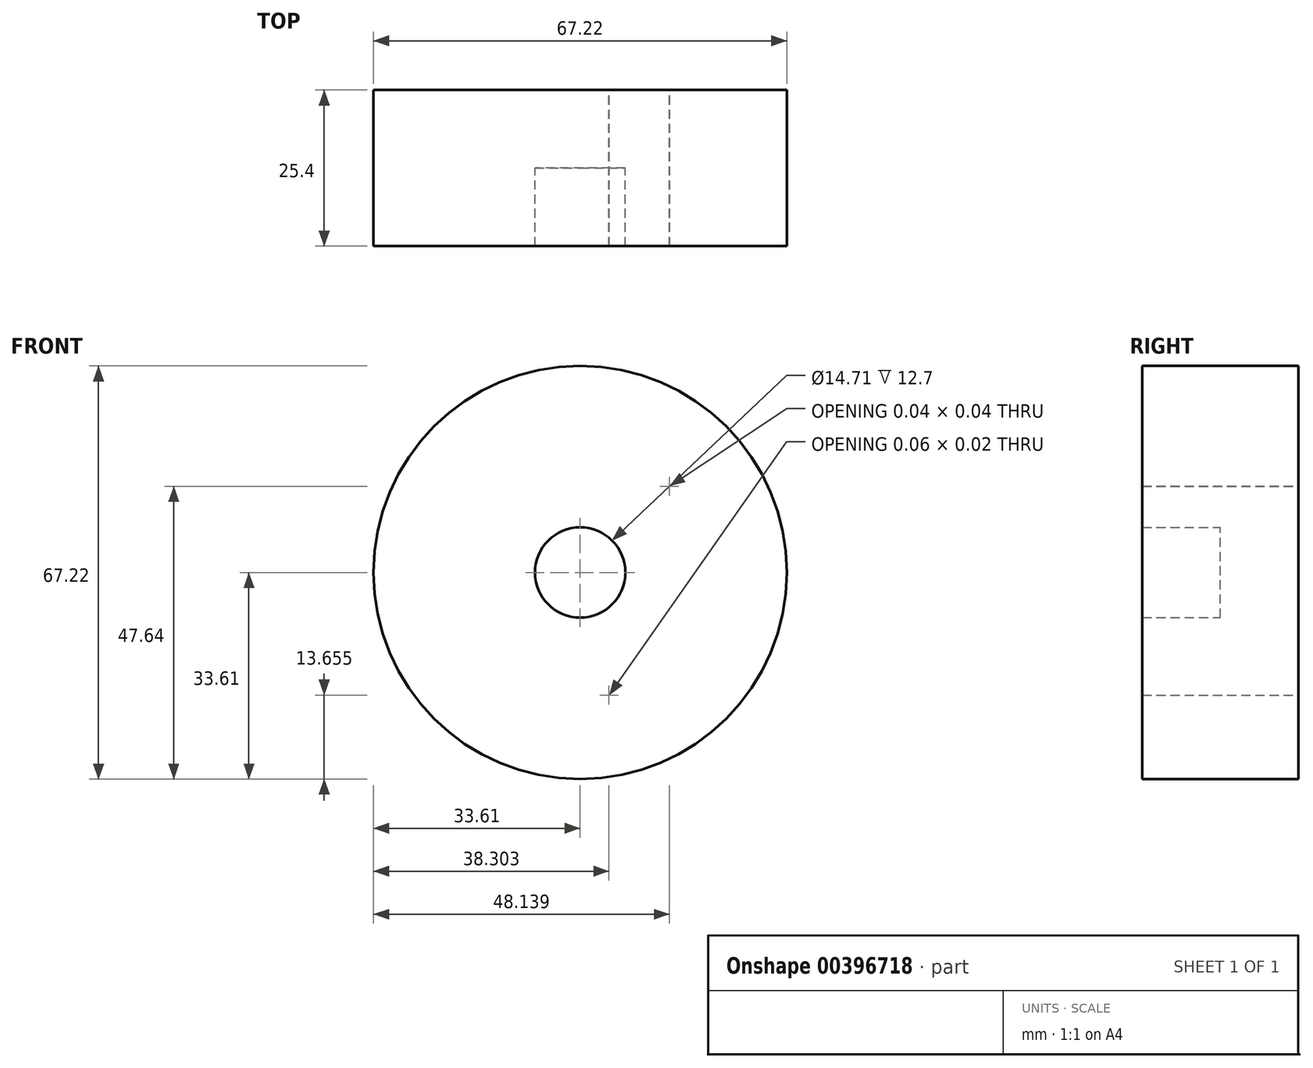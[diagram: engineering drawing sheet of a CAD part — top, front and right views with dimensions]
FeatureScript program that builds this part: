
annotation { "Feature Type Name" : "Feature", "Feature Type Description" : "" }
export const myFeature = defineFeature(function(context is Context, id is Id, definition is map)
    precondition{}
    {
        {
            var Q0;
            Q0=qCreatedBy(makeId("Front.planeOp"),FACE);
            var sketch = newSketch(context, id + "F0", { "sketchPlane" : qUnion([Q0])});
            skCircle(sketch, "E0", {"center": v(0, 0) * mm, "radius": 33.61 * mm});
            skCircle(sketch, "E1", {"center": v(0, 0) * mm, "radius": 7.35 * mm});
            skArc(sketch, "E2", {"start": v(14.55, 14) * mm, "mid": v(14.53, 14.03) * mm, "end": v(14.52, 14.05) * mm});
            skArc(sketch, "E3", {"start": v(14.55, 14) * mm, "mid": v(14.53, 14.03) * mm, "end": v(14.5, 14.05) * mm});
            skArc(sketch, "E4", {"start": v(14.52, 14.05) * mm, "mid": v(14.51, 14.05) * mm, "end": v(14.5, 14.05) * mm});
            skArc(sketch, "E5", {"start": v(4.66, -19.97) * mm, "mid": v(4.7, -19.96) * mm, "end": v(4.72, -19.95) * mm});
            skPoint(sketch, "E6.endSnap0", {"position": v(-19.51, 5.12) * mm});
            skArc(sketch, "E7", {"start": v(4.66, -19.97) * mm, "mid": v(4.7, -19.95) * mm, "end": v(4.72, -19.94) * mm});
            skArc(sketch, "E8", {"start": v(4.72, -19.95) * mm, "mid": v(4.72, -19.95) * mm, "end": v(4.72, -19.94) * mm});
            skPoint(sketch, "E9.orphan", {"position": v(0, 7.35) * mm});
            skPoint(sketch, "E10.end.orphan", {"position": v(18.76, 5.12) * mm});
            skPoint(sketch, "E11.orphan", {"position": v(0, -33.61) * mm});
            skPoint(sketch, "E12.start.orphan", {"position": v(-5.05, -19.97) * mm});
            skSolve(sketch);
        }
        {
            var Q0;
            {var subQ0=sQuery(id+"F0.wireOp",EDGE,"ypr8OIAr-gZSa-dfjQ-iwGS-s2g7RQJyGAwi");Q0=makeQuery(id+"F0.imprint","IMPRINT",FACE,{"disambiguationData":[TD([[makeQuery(id+"F0.imprint","IMPRINT",EDGE,{"derivedFrom":subQ0}),-1.0]])]});}
            var Q1;
            {var subQ0=sQuery(id+"F0.wireOp",EDGE,"pcJwF8Lj-ccY8-LTFF-dTaw-QFjFHTA8a31K");Q1=makeQuery(id+"F0.imprint","IMPRINT",FACE,{"disambiguationData":[TD([[makeQuery(id+"F0.imprint","IMPRINT",EDGE,{"derivedFrom":subQ0}),-1.0]])]});}
            var Q2;
            {var subQ0=sQuery(id+"F0.wireOp",EDGE,"55HTWmI2-19od-qPii-Hjk4-NtNte6FnF2xr");Q2=makeQuery(id+"F0.imprint","IMPRINT",FACE,{"disambiguationData":[TD([[makeQuery(id+"F0.imprint","IMPRINT",EDGE,{"derivedFrom":subQ0}),-1.0]])]});}
            var Q3;
            {var subQ0=sQuery(id+"F0.wireOp",EDGE,"E12");Q3=makeQuery(id+"F0.imprint","IMPRINT",FACE,{"disambiguationData":[TD([[makeQuery(id+"F0.imprint","IMPRINT",EDGE,{"derivedFrom":subQ0}),1.0]])]});}
            var Q4;
            {var subQ0=sQuery(id+"F0.wireOp",EDGE,"1qFRc2v0-qFK7-264P-BVnN-CxCA6gksfMSX");Q4=makeQuery(id+"F0.imprint","IMPRINT",FACE,{"disambiguationData":[TD([[makeQuery(id+"F0.imprint","IMPRINT",EDGE,{"derivedFrom":subQ0}),-1.0]])]});}
            var Q5;
            {var subQ0=sQuery(id+"F0.wireOp",EDGE,"E6");Q5=makeQuery(id+"F0.imprint","IMPRINT",FACE,{"disambiguationData":[TD([[makeQuery(id+"F0.imprint","IMPRINT",EDGE,{"derivedFrom":subQ0}),-1.0]])]});}
            var Q6;
            {var subQ0=sQuery(id+"F0.wireOp",EDGE,"E1");var subQ1=makeQuery(id+"F0.imprint","INTERSECT",VERTEX,{"derivedFrom":[subQ0,sQuery(id+"F0.wireOp",EDGE,"pcJwF8Lj-ccY8-LTFF-dTaw-QFjFHTA8a31K"),sQuery(id+"F0.wireOp",EDGE,"E4")]});Q6=makeQuery(id+"F0.imprint","IMPRINT",FACE,{"disambiguationData":[TD([[makeQuery(id+"F0.imprint","IMPRINT",EDGE,{"disambiguationData":[TD([[subQ1,-1.0]])],"derivedFrom":subQ0}),1.0]])]});}
            extrude(context, id + "F1", {"entities" : qUnion([Q0, Q1, Q2, Q3, Q4, Q5, Q6]), "depth" : 12.7 * mm});
        }
        {
            var Q0;
            Q0 = qSketchRegion(id + "F0", true);
            extrude(context, id + "F2", {"entities" : qUnion([Q0]), "operationType" : NewBodyOperationType.ADD, "depth" : 25.4 * mm});
        }
    });
